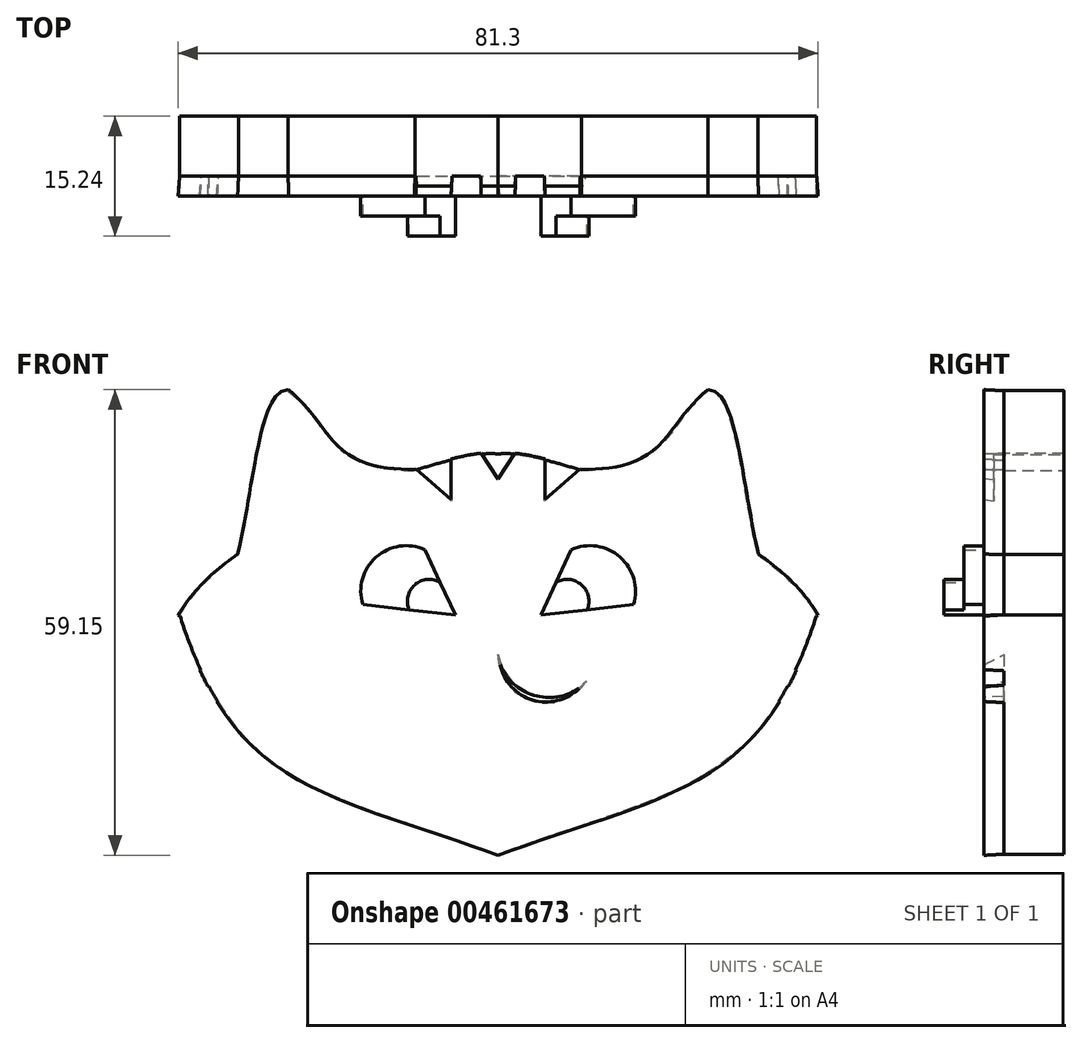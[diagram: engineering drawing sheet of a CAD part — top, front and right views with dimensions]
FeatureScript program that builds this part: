
annotation { "Feature Type Name" : "Feature", "Feature Type Description" : "" }
export const myFeature = defineFeature(function(context is Context, id is Id, definition is map)
    precondition{}
    {
        {
            var Q0;
            Q0=qCreatedBy(makeId("Front.planeOp"),FACE);
            var sketch = newSketch(context, id + "F0", { "sketchPlane" : qUnion([Q0])});
            skFitSpline(sketch, "E0", {"points": [v(0, 20.4) * mm, v(-40.46, 0) * mm], "startDerivative": vector(-12.86, 3.44) * mm, "endDerivative": vector(-19.39, -35.25) * mm});
            skFitSpline(sketch, "E1.MirrorCS", {"points": [v(0, 20.4) * mm, v(40.46, 0) * mm], "startDerivative": vector(12.86, 3.44) * mm, "endDerivative": vector(19.39, -35.25) * mm});
            skFitSpline(sketch, "E2", {"points": [v(-40.46, 0) * mm, v(0, -30.4) * mm], "startDerivative": vector(21.14, -66.24) * mm, "endDerivative": vector(67.82, -24.49) * mm});
            skFitSpline(sketch, "E3.MirrorCS", {"points": [v(40.46, 0) * mm, v(0, -30.4) * mm], "startDerivative": vector(-21.14, -66.24) * mm, "endDerivative": vector(-67.82, -24.49) * mm});
            skFitSpline(sketch, "E4", {"points": [v(-32.98, 7.64) * mm, v(-26.67, 28.46) * mm], "startDerivative": vector(5.7, 22.1) * mm, "endDerivative": vector(10.73, -0.98) * mm});
            skFitSpline(sketch, "E5.MirrorCS", {"points": [v(32.98, 7.64) * mm, v(26.67, 28.46) * mm], "startDerivative": vector(-5.7, 22.1) * mm, "endDerivative": vector(-10.73, -0.98) * mm});
            skFitSpline(sketch, "E6", {"points": [v(-26.67, 28.46) * mm, v(-10.58, 18.35) * mm], "startDerivative": vector(16.59, -13.17) * mm, "endDerivative": vector(33.64, 0.57) * mm});
            skFitSpline(sketch, "E7.MirrorCS", {"points": [v(26.67, 28.46) * mm, v(10.58, 18.35) * mm], "startDerivative": vector(-16.59, -13.17) * mm, "endDerivative": vector(-33.64, 0.57) * mm});
            skSolve(sketch);
        }
        {
            var Q0;
            Q0=qSketchRegion(id+"F0",true);
            extrude(context, id + "F1", {"entities" : qUnion([Q0]), "depth" : 7.62 * mm});
        }
        {
            var Q0;
            Q0=makeQuery(id+"F1.opExtrude","CAP_FACE",FACE,{"disambiguationData":[OSD([sQuery(id+"F0.wireOp",EDGE,"E0"),sQuery(id+"F0.wireOp",EDGE,"E1.MirrorCS"),sQuery(id+"F0.wireOp",EDGE,"E2"),sQuery(id+"F0.wireOp",EDGE,"E3.MirrorCS"),sQuery(id+"F0.wireOp",EDGE,"E4"),sQuery(id+"F0.wireOp",EDGE,"E5.MirrorCS"),sQuery(id+"F0.wireOp",EDGE,"E6"),sQuery(id+"F0.wireOp",EDGE,"E7.MirrorCS")])],"isStart":false});
            var sketch = newSketch(context, id + "F2", { "sketchPlane" : qUnion([Q0])});
            skLineSegment(sketch, "E8", {"start": v(-5.44, 0) * mm, "end": v(-9.27, 8.25) * mm});
            skLineSegment(sketch, "E9", {"start": v(-5.44, 0) * mm, "end": v(-22.3, 1.85) * mm});
            skArc(sketch, "E10", {"start": v(-9.27, 8.25) * mm, "mid": v(-19.05, 11.7) * mm, "end": v(-22.3, 1.85) * mm});
            skLineSegment(sketch, "E11.MirrorCS", {"start": v(5.44, 0) * mm, "end": v(9.27, 8.25) * mm});
            skArc(sketch, "E12.MirrorCS", {"start": v(9.27, 8.25) * mm, "mid": v(19.05, 11.7) * mm, "end": v(22.3, 1.85) * mm});
            skLineSegment(sketch, "E13.MirrorCS", {"start": v(5.44, 0) * mm, "end": v(22.3, 1.85) * mm});
            skFitSpline(sketch, "E14", {"points": [v(-2.88, 0) * mm, v(2.72, 0) * mm, v(0, -4.15) * mm, v(-2.88, 0) * mm]});
            skSolve(sketch);
        }
        {
            var Q0;
            Q0=qSketchRegion(id+"F2",true);
            extrude(context, id + "F3", {"entities" : qUnion([Q0]), "operationType" : NewBodyOperationType.ADD, "depth" : 2.54 * mm});
        }
        {
            var Q0;
            Q0=makeQuery(id+"F3.opExtrude","CAP_FACE",FACE,{"disambiguationData":[OSD([sQuery(id+"F2.wireOp",EDGE,"E8"),sQuery(id+"F2.wireOp",EDGE,"E9"),sQuery(id+"F2.wireOp",EDGE,"E10")])],"isStart":false});
            var sketch = newSketch(context, id + "F4", { "sketchPlane" : qUnion([Q0])});
            skArc(sketch, "E15", {"start": v(-9.27, 8.25) * mm, "mid": v(-15.49, 7.34) * mm, "end": v(-17.19, 1.3) * mm});
            skArc(sketch, "E16.MirrorCS", {"start": v(9.27, 8.25) * mm, "mid": v(15.49, 7.34) * mm, "end": v(17.19, 1.3) * mm});
            skLineSegment(sketch, "E17", {"start": v(-9.27, 8.25) * mm, "end": v(-5.44, 0) * mm});
            skLineSegment(sketch, "E18", {"start": v(-5.44, 0) * mm, "end": v(-17.19, 1.3) * mm});
            skLineSegment(sketch, "E19.MirrorCS", {"start": v(9.27, 8.25) * mm, "end": v(5.44, 0) * mm});
            skLineSegment(sketch, "E20.MirrorCS", {"start": v(5.44, 0) * mm, "end": v(17.19, 1.3) * mm});
            skSolve(sketch);
        }
        {
            var Q0;
            Q0=qSketchRegion(id+"F4",true);
            extrude(context, id + "F5", {"entities" : qUnion([Q0]), "operationType" : NewBodyOperationType.ADD, "depth" : 2.54 * mm});
        }
        {
            var Q0;
            Q0=makeQuery(id+"F5.opExtrude","CAP_FACE",FACE,{"disambiguationData":[OSD([sQuery(id+"F4.wireOp",EDGE,"E15"),sQuery(id+"F4.wireOp",EDGE,"E17"),sQuery(id+"F4.wireOp",EDGE,"E18")])],"isStart":false});
            var sketch = newSketch(context, id + "F6", { "sketchPlane" : qUnion([Q0])});
            skArc(sketch, "E21", {"start": v(-7.35, 4.12) * mm, "mid": v(-10.59, 3.81) * mm, "end": v(-11.31, 0.65) * mm});
            skPoint(sketch, "E21.midSnap0", {"position": v(-11.31, 0.65) * mm});
            skPoint(sketch, "E21.midSnap1", {"position": v(-7.35, 4.12) * mm});
            skArc(sketch, "E22.MirrorCS", {"start": v(7.35, 4.12) * mm, "mid": v(10.59, 3.81) * mm, "end": v(11.31, 0.65) * mm});
            skLineSegment(sketch, "E23", {"start": v(-7.35, 4.12) * mm, "end": v(-5.44, 0) * mm});
            skLineSegment(sketch, "E24", {"start": v(-5.44, 0) * mm, "end": v(-11.31, 0.65) * mm});
            skLineSegment(sketch, "E25.MirrorCS", {"start": v(7.35, 4.12) * mm, "end": v(5.44, 0) * mm});
            skLineSegment(sketch, "E26.MirrorCS", {"start": v(5.44, 0) * mm, "end": v(11.31, 0.65) * mm});
            skSolve(sketch);
        }
        {
            var Q0;
            Q0=qSketchRegion(id+"F6",true);
            extrude(context, id + "F7", {"entities" : qUnion([Q0]), "operationType" : NewBodyOperationType.ADD, "depth" : 2.54 * mm});
        }
        {
            var Q0;
            Q0=makeQuery(id+"F1.opExtrude","CAP_FACE",FACE,{"disambiguationData":[OSD([sQuery(id+"F0.wireOp",EDGE,"E0"),sQuery(id+"F0.wireOp",EDGE,"E1.MirrorCS"),sQuery(id+"F0.wireOp",EDGE,"E2"),sQuery(id+"F0.wireOp",EDGE,"E3.MirrorCS"),sQuery(id+"F0.wireOp",EDGE,"E4"),sQuery(id+"F0.wireOp",EDGE,"E5.MirrorCS"),sQuery(id+"F0.wireOp",EDGE,"E6"),sQuery(id+"F0.wireOp",EDGE,"E7.MirrorCS")])],"isStart":false});
            var sketch = newSketch(context, id + "F8", { "sketchPlane" : qUnion([Q0])});
            skLineSegment(sketch, "E27", {"start": v(-40.46, 0) * mm, "end": v(-21.36, -7.1) * mm});
            skLineSegment(sketch, "E28", {"start": v(-21.36, -7.1) * mm, "end": v(-37.73, -7.1) * mm});
            skLineSegment(sketch, "E29", {"start": v(-36.8, -8.96) * mm, "end": v(-26.62, -11.15) * mm});
            skLineSegment(sketch, "E30", {"start": v(-26.62, -11.15) * mm, "end": v(-35.54, -11.15) * mm});
            skLineSegment(sketch, "E31.MirrorCS", {"start": v(40.46, 0) * mm, "end": v(21.36, -7.1) * mm});
            skLineSegment(sketch, "E32.MirrorCS", {"start": v(21.36, -7.1) * mm, "end": v(37.73, -7.1) * mm});
            skLineSegment(sketch, "E33.MirrorCS", {"start": v(36.8, -8.96) * mm, "end": v(26.62, -11.15) * mm});
            skLineSegment(sketch, "E34.MirrorCS", {"start": v(26.62, -11.15) * mm, "end": v(35.54, -11.15) * mm});
            skLineSegment(sketch, "E35", {"start": v(-10.44, 18.4) * mm, "end": v(-5.85, 14.33) * mm});
            skLineSegment(sketch, "E36", {"start": v(-5.85, 14.33) * mm, "end": v(-5.85, 19.7) * mm});
            skLineSegment(sketch, "E37", {"start": v(-2.22, 20.4) * mm, "end": v(0, 17.03) * mm});
            skLineSegment(sketch, "E38.MirrorCS", {"start": v(2.22, 20.4) * mm, "end": v(0, 17.03) * mm});
            skLineSegment(sketch, "E39.MirrorCS", {"start": v(5.85, 14.33) * mm, "end": v(5.85, 19.7) * mm});
            skLineSegment(sketch, "E40.MirrorCS", {"start": v(10.44, 18.4) * mm, "end": v(5.85, 14.33) * mm});
            skSolve(sketch);
        }
        {
            var Q0;
            {var subQ0=sQuery(id+"F8.wireOp",EDGE,"E27");Q0=makeQuery(id+"F8.imprint","IMPRINT",FACE,{"disambiguationData":[TD([[makeQuery(id+"F8.imprint","IMPRINT",EDGE,{"derivedFrom":subQ0}),-1.0]])]});}
            var Q1;
            {var subQ0=sQuery(id+"F8.wireOp",EDGE,"E29");Q1=makeQuery(id+"F8.imprint","IMPRINT",FACE,{"disambiguationData":[TD([[makeQuery(id+"F8.imprint","IMPRINT",EDGE,{"derivedFrom":subQ0}),-1.0]])]});}
            var Q2;
            {var subQ0=sQuery(id+"F8.wireOp",EDGE,"E31.MirrorCS");Q2=makeQuery(id+"F8.imprint","IMPRINT",FACE,{"disambiguationData":[TD([[makeQuery(id+"F8.imprint","IMPRINT",EDGE,{"derivedFrom":subQ0}),1.0]])]});}
            var Q3;
            {var subQ0=sQuery(id+"F8.wireOp",EDGE,"E34.MirrorCS");Q3=makeQuery(id+"F8.imprint","IMPRINT",FACE,{"disambiguationData":[TD([[makeQuery(id+"F8.imprint","IMPRINT",EDGE,{"derivedFrom":subQ0}),1.0]])]});}
            extrude(context, id + "F9", {"entities" : qUnion([Q0, Q1, Q2, Q3]), "operationType" : NewBodyOperationType.ADD, "depth" : 2.54 * mm});
        }
        {
            var Q0;
            {var subQ0=sQuery(id+"F8.wireOp",EDGE,"E35");Q0=makeQuery(id+"F8.imprint","IMPRINT",FACE,{"disambiguationData":[TD([[makeQuery(id+"F8.imprint","IMPRINT",EDGE,{"derivedFrom":subQ0}),1.0]])]});}
            var Q1;
            {var subQ0=sQuery(id+"F8.wireOp",EDGE,"E37");Q1=makeQuery(id+"F8.imprint","IMPRINT",FACE,{"disambiguationData":[TD([[makeQuery(id+"F8.imprint","IMPRINT",EDGE,{"derivedFrom":subQ0}),1.0]])]});}
            var Q2;
            {var subQ0=sQuery(id+"F8.wireOp",EDGE,"E39.MirrorCS");Q2=makeQuery(id+"F8.imprint","IMPRINT",FACE,{"disambiguationData":[TD([[makeQuery(id+"F8.imprint","IMPRINT",EDGE,{"derivedFrom":subQ0}),-1.0]])]});}
            extrude(context, id + "F10", {"entities" : qUnion([Q0, Q1, Q2]), "operationType" : NewBodyOperationType.ADD, "depth" : 1.27 * mm});
        }
        {
            var Q0;
            Q0=makeQuery(id+"F1.opExtrude","CAP_FACE",FACE,{"disambiguationData":[OSD([sQuery(id+"F0.wireOp",EDGE,"E0"),sQuery(id+"F0.wireOp",EDGE,"E1.MirrorCS"),sQuery(id+"F0.wireOp",EDGE,"E2"),sQuery(id+"F0.wireOp",EDGE,"E3.MirrorCS"),sQuery(id+"F0.wireOp",EDGE,"E4"),sQuery(id+"F0.wireOp",EDGE,"E5.MirrorCS"),sQuery(id+"F0.wireOp",EDGE,"E6"),sQuery(id+"F0.wireOp",EDGE,"E7.MirrorCS")])],"isStart":false});
            var sketch = newSketch(context, id + "F11", { "sketchPlane" : qUnion([Q0])});
            skCircle(sketch, "E41", {"center": v(43.28, 30.93) * mm, "radius": 6.17 * mm});
            skSolve(sketch);
        }
        {
            var Q0;
            Q0=makeQuery(id+"F11.imprint","IMPRINT",FACE,{"disambiguationData":[TD([[makeQuery(id+"F11.imprint","IMPRINT",EDGE,{"derivedFrom":sQuery(id+"F11.wireOp",EDGE,"E41")}),1.0]])]});
            extrude(context, id + "F12", {"entities" : qUnion([Q0]), "operationType" : NewBodyOperationType.REMOVE, "oppositeDirection" : true, "depth" : 25.4 * mm, "hasSecondDirection" : true, "secondDirectionOppositeDirection" : false, "secondDirectionDepth" : 41 * mm});
        }
        {
            var Q0;
            Q0=makeQuery(id+"F1.opExtrude","CAP_FACE",FACE,{"disambiguationData":[OSD([sQuery(id+"F0.wireOp",EDGE,"E0"),sQuery(id+"F0.wireOp",EDGE,"E1.MirrorCS"),sQuery(id+"F0.wireOp",EDGE,"E2"),sQuery(id+"F0.wireOp",EDGE,"E3.MirrorCS"),sQuery(id+"F0.wireOp",EDGE,"E4"),sQuery(id+"F0.wireOp",EDGE,"E5.MirrorCS"),sQuery(id+"F0.wireOp",EDGE,"E6"),sQuery(id+"F0.wireOp",EDGE,"E7.MirrorCS")])],"isStart":false});
            var sketch = newSketch(context, id + "F13", { "sketchPlane" : qUnion([Q0])});
            skArc(sketch, "E42", {"start": v(-11.2, -8.4) * mm, "mid": v(-4.33, -10.94) * mm, "end": v(0, -5.04) * mm});
            skArc(sketch, "E43", {"start": v(-11.2, -8.4) * mm, "mid": v(-4.59, -10.1) * mm, "end": v(0, -5.04) * mm});
            skArc(sketch, "E44.MirrorCS", {"start": v(11.2, -8.4) * mm, "mid": v(4.59, -10.1) * mm, "end": v(0, -5.04) * mm});
            skArc(sketch, "E45.MirrorCS", {"start": v(11.2, -8.4) * mm, "mid": v(4.33, -10.94) * mm, "end": v(0, -5.04) * mm});
            skFitSpline(sketch, "E46", {"points": [v(-3.21, -10.48) * mm, v(0, -16.1) * mm], "startDerivative": vector(-1.35, -10.4) * mm, "endDerivative": vector(5.35, -1.67) * mm});
            skFitSpline(sketch, "E47.MirrorCS", {"points": [v(3.21, -10.48) * mm, v(0, -16.1) * mm], "startDerivative": vector(1.35, -10.4) * mm, "endDerivative": vector(-5.35, -1.67) * mm});
            skSolve(sketch);
        }
        {
            var Q0;
            {var subQ0=sQuery(id+"F13.wireOp",EDGE,"E46");Q0=makeQuery(id+"F13.imprint","IMPRINT",FACE,{"disambiguationData":[TD([[makeQuery(id+"F13.imprint","IMPRINT",EDGE,{"derivedFrom":subQ0}),1.0]])]});}
            var Q1;
            {var subQ1=sQuery(id+"F13.wireOp",EDGE,"E44.MirrorCS");Q1=makeQuery(id+"F13.imprint","IMPRINT",FACE,{"disambiguationData":[TD([[makeQuery(id+"F13.imprint","IMPRINT",EDGE,{"derivedFrom":subQ1}),1.0]])]});}
            var Q2;
            {var subQ0=sQuery(id+"F13.wireOp",EDGE,"E43");Q2=makeQuery(id+"F13.imprint","IMPRINT",FACE,{"disambiguationData":[TD([[makeQuery(id+"F13.imprint","IMPRINT",EDGE,{"derivedFrom":subQ0}),-1.0]])]});}
            extrude(context, id + "F14", {"entities" : qUnion([Q0, Q1, Q2]), "operationType" : NewBodyOperationType.ADD, "depth" : 2.54 * mm, "hasDraft" : true, "draftAngle" : 3 * degree});
        }
        {
            var Q0;
            {var subQ0=sQuery(id+"F13.wireOp",EDGE,"E46");Q0=makeQuery(id+"F13.imprint","IMPRINT",FACE,{"disambiguationData":[TD([[makeQuery(id+"F13.imprint","IMPRINT",EDGE,{"derivedFrom":subQ0}),1.0]])]});}
            extrude(context, id + "F15", {"entities" : qUnion([Q0]), "operationType" : NewBodyOperationType.ADD, "depth" : 2.54 * mm});
        }
        {
            var Q0;
            {var subQ1=sQuery(id+"F13.wireOp",EDGE,"E44.MirrorCS");Q0=makeQuery(id+"F13.imprint","IMPRINT",FACE,{"disambiguationData":[TD([[makeQuery(id+"F13.imprint","IMPRINT",EDGE,{"derivedFrom":subQ1}),1.0]])]});}
            extrude(context, id + "F16", {"entities" : qUnion([Q0]), "operationType" : NewBodyOperationType.ADD, "depth" : 2.54 * mm});
        }
        {
            var Q0;
            {var subQ0=sQuery(id+"F13.wireOp",EDGE,"E43");Q0=makeQuery(id+"F13.imprint","IMPRINT",FACE,{"disambiguationData":[TD([[makeQuery(id+"F13.imprint","IMPRINT",EDGE,{"derivedFrom":subQ0}),-1.0]])]});}
            extrude(context, id + "F17", {"entities" : qUnion([Q0]), "operationType" : NewBodyOperationType.ADD, "depth" : 2.54 * mm});
        }
    });
